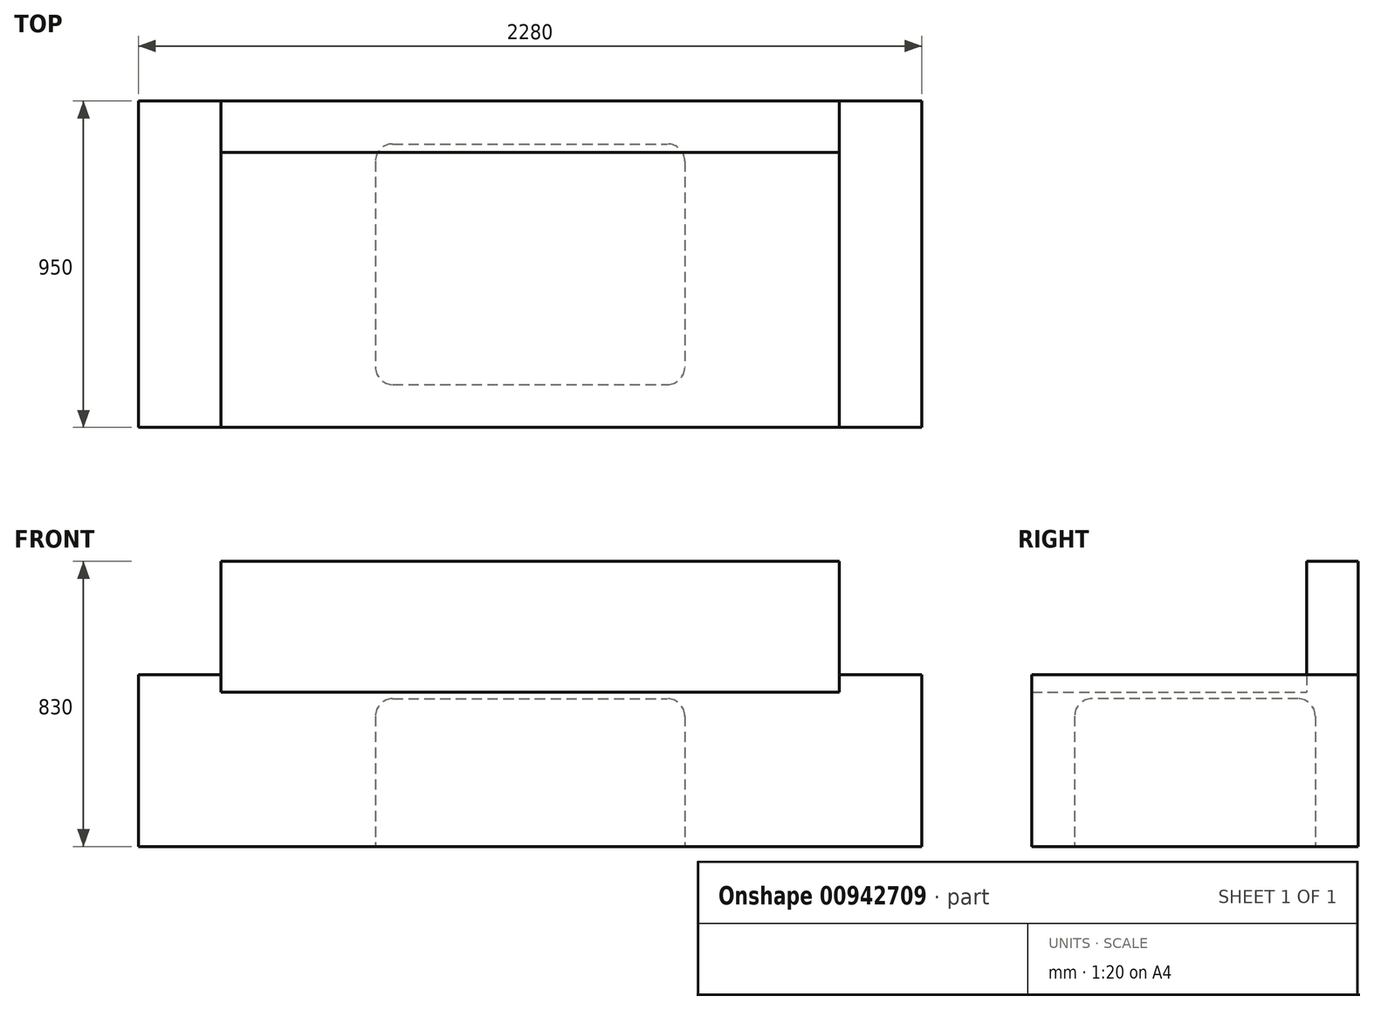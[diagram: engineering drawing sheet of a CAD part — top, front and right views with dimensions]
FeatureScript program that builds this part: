
annotation { "Feature Type Name" : "Feature", "Feature Type Description" : "" }
export const myFeature = defineFeature(function(context is Context, id is Id, definition is map)
    precondition{}
    {
        {
            var Q0;
            Q0=qCreatedBy(makeId("Top.planeOp"),FACE);
            var sketch = newSketch(context, id + "F0", { "sketchPlane" : qUnion([Q0])});
            skLineSegment(sketch, "E0.bottom", {"start": v(-1140, -475) * mm, "end": v(1140, -475) * mm});
            skLineSegment(sketch, "E0.top", {"start": v(-1140, 475) * mm, "end": v(1140, 475) * mm});
            skLineSegment(sketch, "E0.left", {"start": v(-1140, -475) * mm, "end": v(-1140, 475) * mm});
            skLineSegment(sketch, "E0.right", {"start": v(1140, -475) * mm, "end": v(1140, 475) * mm});
            skLineSegment(sketch, "E1", {"start": v(-1140, 0) * mm, "end": v(0, 0) * mm, "construction": true});
            skLineSegment(sketch, "E2", {"start": v(0, 0) * mm, "end": v(1140, 0) * mm, "construction": true});
            skLineSegment(sketch, "E3", {"start": v(0, -475) * mm, "end": v(0, 0) * mm, "construction": true});
            skLineSegment(sketch, "E4", {"start": v(0, 0) * mm, "end": v(0, 475) * mm, "construction": true});
            skLineSegment(sketch, "E5.bottom", {"start": v(-900, -475) * mm, "end": v(900, -475) * mm});
            skLineSegment(sketch, "E5.top", {"start": v(-900, 325) * mm, "end": v(900, 325) * mm});
            skLineSegment(sketch, "E5.left", {"start": v(-900, -475) * mm, "end": v(-900, 325) * mm});
            skLineSegment(sketch, "E5.right", {"start": v(900, -475) * mm, "end": v(900, 325) * mm});
            skLineSegment(sketch, "E6", {"start": v(-900, 325) * mm, "end": v(-900, 475) * mm});
            skLineSegment(sketch, "E7", {"start": v(900, 325) * mm, "end": v(900, 475) * mm});
            skSolve(sketch);
        }
        {
            var Q0;
            {var subQ3=sQuery(id+"F0.wireOp",EDGE,"E0.left");Q0=makeQuery(id+"F0.imprint","IMPRINT",FACE,{"disambiguationData":[TD([[makeQuery(id+"F0.imprint","IMPRINT",EDGE,{"derivedFrom":subQ3}),-1.0]])]});}
            var Q1;
            {var subQ1=sQuery(id+"F0.wireOp",EDGE,"E0.right");Q1=makeQuery(id+"F0.imprint","IMPRINT",FACE,{"disambiguationData":[TD([[makeQuery(id+"F0.imprint","IMPRINT",EDGE,{"derivedFrom":subQ1}),1.0]])]});}
            extrude(context, id + "F1", {"entities" : qUnion([Q0, Q1]), "depth" : 500 * mm, "offsetDistance" : 25 * mm});
        }
        {
            var Q0;
            Q0=makeQuery(id+"F0.imprint","IMPRINT",FACE,{"disambiguationData":[TD([[makeQuery(id+"F0.imprint","IMPRINT",EDGE,{"derivedFrom":sQuery(id+"F0.wireOp",EDGE,"E5.top")}),-1.0]])]});
            extrude(context, id + "F2", {"entities" : qUnion([Q0]), "operationType" : NewBodyOperationType.ADD, "depth" : 450 * mm, "offsetDistance" : 25 * mm});
        }
        {
            var Q0;
            Q0=makeQuery(id+"F0.imprint","IMPRINT",FACE,{"disambiguationData":[TD([[makeQuery(id+"F0.imprint","IMPRINT",EDGE,{"derivedFrom":sQuery(id+"F0.wireOp",EDGE,"E5.top")}),1.0]])]});
            extrude(context, id + "F3", {"entities" : qUnion([Q0]), "operationType" : NewBodyOperationType.ADD, "depth" : 830 * mm, "offsetDistance" : 25 * mm});
        }
        {
            var Q0;
            Q0=qCreatedBy(makeId("Top.planeOp"),FACE);
            var sketch = newSketch(context, id + "F4", { "sketchPlane" : qUnion([Q0])});
            skLineSegment(sketch, "E8.bottom", {"start": v(-450, 350) * mm, "end": v(450, 350) * mm});
            skLineSegment(sketch, "E8.top", {"start": v(-450, -350) * mm, "end": v(450, -350) * mm});
            skLineSegment(sketch, "E8.left", {"start": v(-450, 350) * mm, "end": v(-450, -350) * mm});
            skLineSegment(sketch, "E8.right", {"start": v(450, 350) * mm, "end": v(450, -350) * mm});
            skLineSegment(sketch, "E9", {"start": v(-450, 0) * mm, "end": v(0, 0) * mm, "construction": true});
            skLineSegment(sketch, "E10", {"start": v(0, 0) * mm, "end": v(450, 0) * mm, "construction": true});
            skLineSegment(sketch, "E11", {"start": v(0, -350) * mm, "end": v(0, 0) * mm, "construction": true});
            skLineSegment(sketch, "E12", {"start": v(0, 0) * mm, "end": v(0, 350) * mm, "construction": true});
            skSolve(sketch);
        }
        {
            var Q0;
            Q0=makeQuery(id+"F4.imprint","IMPRINT",FACE,{"disambiguationData":[TD([[makeQuery(id+"F4.imprint","IMPRINT",EDGE,{"derivedFrom":sQuery(id+"F4.wireOp",EDGE,"E8.bottom")}),-1.0]])]});
            extrude(context, id + "F5", {"entities" : qUnion([Q0]), "depth" : 430 * mm, "offsetDistance" : 25 * mm});
        }
        {
            var Q0;
            Q0=makeQuery(id+"F5.opExtrude","CAP_FACE",FACE,{"disambiguationData":[OSD([sQuery(id+"F4.wireOp",EDGE,"E8.bottom"),sQuery(id+"F4.wireOp",EDGE,"E8.top"),sQuery(id+"F4.wireOp",EDGE,"E8.left"),sQuery(id+"F4.wireOp",EDGE,"E8.right")])],"isStart":false});
            var Q1;
            Q1=makeQuery(id+"F5.opExtrude","SWEPT_EDGE",EDGE,{"disambiguationData":[OSD([sQuery(id+"F4.wireOp",EDGE,"E8.top"),sQuery(id+"F4.wireOp",EDGE,"E8.left")])]});
            var Q2;
            Q2=makeQuery(id+"F5.opExtrude","SWEPT_EDGE",EDGE,{"disambiguationData":[OSD([sQuery(id+"F4.wireOp",EDGE,"E8.top"),sQuery(id+"F4.wireOp",EDGE,"E8.right")])]});
            var Q3;
            Q3=makeQuery(id+"F5.opExtrude","SWEPT_EDGE",EDGE,{"disambiguationData":[OSD([sQuery(id+"F4.wireOp",EDGE,"E8.bottom"),sQuery(id+"F4.wireOp",EDGE,"E8.right")])]});
            var Q4;
            Q4=makeQuery(id+"F5.opExtrude","SWEPT_EDGE",EDGE,{"disambiguationData":[OSD([sQuery(id+"F4.wireOp",EDGE,"E8.bottom"),sQuery(id+"F4.wireOp",EDGE,"E8.left")])]});
            fillet(context, id + "F6", {"entities" : qUnion([Q0, Q1, Q2, Q3, Q4]), "tangentPropagation" : true, "radius" : 50 * mm, "defaultsChanged" : false, "vertexSettings" : [], "allowEdgeOverflow" : false});
        }
    });
